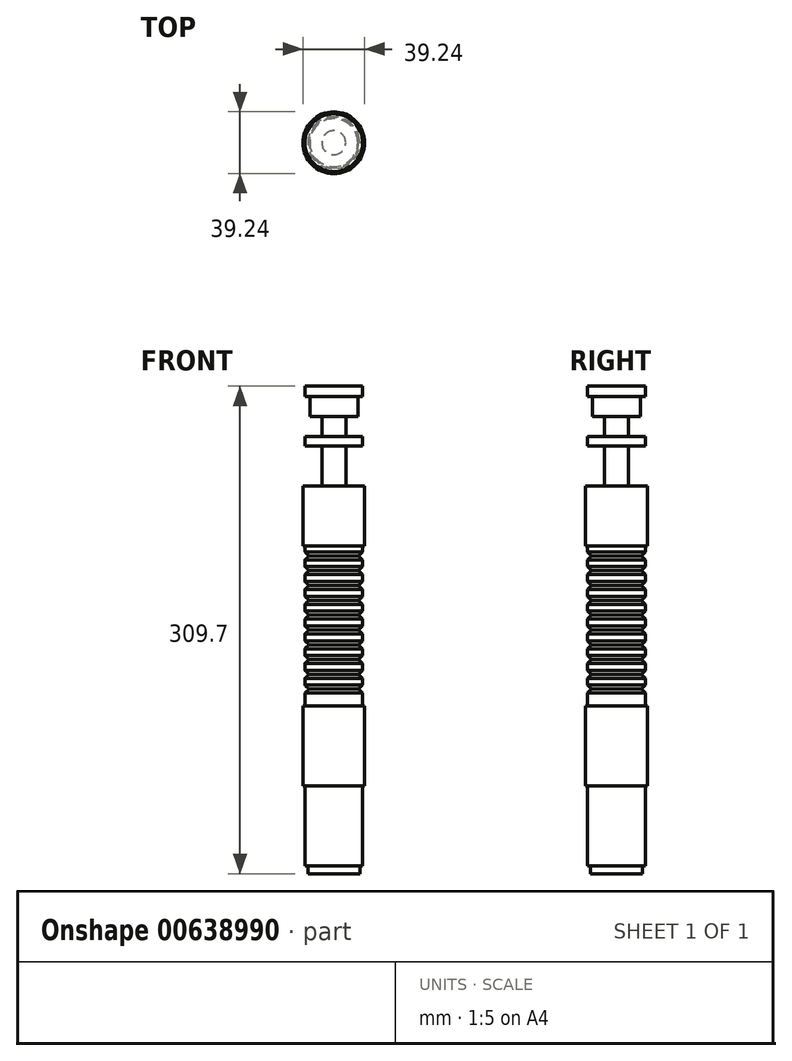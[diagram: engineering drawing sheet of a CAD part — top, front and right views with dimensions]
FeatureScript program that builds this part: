
annotation { "Feature Type Name" : "Feature", "Feature Type Description" : "" }
export const myFeature = defineFeature(function(context is Context, id is Id, definition is map)
    precondition{}
    {
        {
            var Q0;
            Q0=qCreatedBy(makeId("Front.planeOp"),FACE);
            var sketch = newSketch(context, id + "F0", { "sketchPlane" : qUnion([Q0])});
            skLineSegment(sketch, "E0", {"start": v(0, 169.93) * mm, "end": v(18.35, 169.93) * mm});
            skLineSegment(sketch, "E1", {"start": v(18.35, 169.93) * mm, "end": v(18.35, 163.4) * mm});
            skLineSegment(sketch, "E2", {"start": v(18.35, 163.4) * mm, "end": v(15.24, 163.4) * mm});
            skLineSegment(sketch, "E3", {"start": v(15.24, 163.4) * mm, "end": v(15.24, 150.7) * mm});
            skLineSegment(sketch, "E4", {"start": v(15.24, 150.7) * mm, "end": v(7.62, 150.7) * mm});
            skLineSegment(sketch, "E5", {"start": v(7.62, 150.7) * mm, "end": v(7.62, 138) * mm});
            skLineSegment(sketch, "E6", {"start": v(7.62, 138) * mm, "end": v(18.35, 138) * mm});
            skLineSegment(sketch, "E7", {"start": v(18.35, 138) * mm, "end": v(18.35, 132) * mm});
            skLineSegment(sketch, "E8", {"start": v(18.35, 132) * mm, "end": v(7.62, 132) * mm});
            skLineSegment(sketch, "E9", {"start": v(7.62, 132) * mm, "end": v(7.62, 106.6) * mm});
            skLineSegment(sketch, "E10", {"start": v(7.62, 106.6) * mm, "end": v(18.35, 106.6) * mm});
            skLineSegment(sketch, "E11", {"start": v(18.35, 68.5) * mm, "end": v(18.35, -33.1) * mm});
            skLineSegment(sketch, "E12", {"start": v(0, -139.77) * mm, "end": v(0, 169.93) * mm});
            skLineSegment(sketch, "E13", {"start": v(18.35, -134.7) * mm, "end": v(16.5, -134.7) * mm});
            skLineSegment(sketch, "E14", {"start": v(16.51, -134.7) * mm, "end": v(16.51, -139.77) * mm});
            skLineSegment(sketch, "E15", {"start": v(0, -139.77) * mm, "end": v(16.5, -139.77) * mm});
            skPoint(sketch, "E16", {"position": v(18.35, -33.1) * mm});
            skLineSegment(sketch, "E17", {"start": v(18.35, -33.1) * mm, "end": v(19.62, -33.1) * mm});
            skLineSegment(sketch, "E18", {"start": v(19.62, -33.1) * mm, "end": v(19.62, -83.9) * mm});
            skLineSegment(sketch, "E19", {"start": v(19.62, -83.9) * mm, "end": v(18.35, -83.9) * mm});
            skLineSegment(sketch, "E20.trimOffspring", {"start": v(18.35, -83.9) * mm, "end": v(18.35, -134.7) * mm});
            skLineSegment(sketch, "E21", {"start": v(18.35, 64.7) * mm, "end": v(15.81, 62.16) * mm});
            skLineSegment(sketch, "E22", {"start": v(15.81, 62.16) * mm, "end": v(18.35, 59.62) * mm});
            skLineSegment(sketch, "E23.1.0.0", {"start": v(18.35, 55.29) * mm, "end": v(15.81, 52.75) * mm});
            skLineSegment(sketch, "E23.1.0.1", {"start": v(15.81, 52.75) * mm, "end": v(18.35, 50.2) * mm});
            skLineSegment(sketch, "E23.2.0.0", {"start": v(18.35, 45.88) * mm, "end": v(15.81, 43.34) * mm});
            skLineSegment(sketch, "E23.2.0.1", {"start": v(15.81, 43.34) * mm, "end": v(18.35, 40.8) * mm});
            skLineSegment(sketch, "E23.3.0.0", {"start": v(18.35, 36.47) * mm, "end": v(15.81, 33.93) * mm});
            skLineSegment(sketch, "E23.3.0.1", {"start": v(15.81, 33.93) * mm, "end": v(18.35, 31.39) * mm});
            skLineSegment(sketch, "E23.4.0.0", {"start": v(18.35, 27.06) * mm, "end": v(15.81, 24.52) * mm});
            skLineSegment(sketch, "E23.4.0.1", {"start": v(15.81, 24.52) * mm, "end": v(18.35, 21.98) * mm});
            skLineSegment(sketch, "E23.5.0.0", {"start": v(18.35, 17.65) * mm, "end": v(15.81, 15.1) * mm});
            skLineSegment(sketch, "E23.5.0.1", {"start": v(15.81, 15.1) * mm, "end": v(18.35, 12.57) * mm});
            skLineSegment(sketch, "E23.6.0.0", {"start": v(18.35, 8.24) * mm, "end": v(15.81, 5.7) * mm});
            skLineSegment(sketch, "E23.6.0.1", {"start": v(15.81, 5.7) * mm, "end": v(18.35, 3.16) * mm});
            skLineSegment(sketch, "E23.7.0.0", {"start": v(18.35, -1.17) * mm, "end": v(15.81, -3.7) * mm});
            skLineSegment(sketch, "E23.7.0.1", {"start": v(15.81, -3.7) * mm, "end": v(18.35, -6.25) * mm});
            skLineSegment(sketch, "E23.8.0.0", {"start": v(18.35, -10.58) * mm, "end": v(15.81, -13.12) * mm});
            skLineSegment(sketch, "E23.8.0.1", {"start": v(15.81, -13.12) * mm, "end": v(18.35, -15.66) * mm});
            skLineSegment(sketch, "E23.9.0.0", {"start": v(18.35, -19.99) * mm, "end": v(15.81, -22.53) * mm});
            skLineSegment(sketch, "E23.9.0.1", {"start": v(15.81, -22.53) * mm, "end": v(18.35, -25.07) * mm});
            skLineSegment(sketch, "E23.direction1", {"start": v(18.35, 59.62) * mm, "end": v(18.35, 50.2) * mm, "construction": true});
            skLineSegment(sketch, "E24", {"start": v(18.35, 68.5) * mm, "end": v(19.62, 68.5) * mm});
            skLineSegment(sketch, "E25", {"start": v(19.62, 68.5) * mm, "end": v(19.62, 106.6) * mm});
            skLineSegment(sketch, "E26", {"start": v(18.35, 106.6) * mm, "end": v(19.62, 106.6) * mm});
            skSolve(sketch);
        }
        {
            var Q0;
            Q0=makeQuery(id+"F0.imprint","IMPRINT",FACE,{"disambiguationData":[TD([[makeQuery(id+"F0.imprint","IMPRINT",EDGE,{"derivedFrom":sQuery(id+"F0.wireOp",EDGE,"E0")}),-1.0]])]});
            var Q1;
            Q1=sQuery(id+"F0.wireOp",EDGE,"E12");
            revolve(context, id + "F1", {"entities" : qUnion([Q0]), "axis" : qUnion([Q1]), "revolveType" : RevolveType.FULL});
        }
    });
